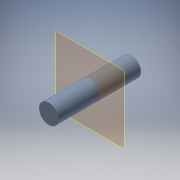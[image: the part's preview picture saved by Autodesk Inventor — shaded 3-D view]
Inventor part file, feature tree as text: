
AUTODESK INVENTOR PART (.ipt)
format: ipt  version: 2019 (Build 230136000, 136)  size: 96,256 bytes
history: native  units: mm
features: other x4, extrude x1, sketch x1, reference x1
ambient origin geometry x8: Origin, YZ Plane, XZ Plane, XY Plane, X Axis, Y Axis, Z Axis, Center Point
bodies: Body1 (feature_tree)
feature tree (7):
  other  "作業平面1"
  extrude  "押し出し2"  Depth=0.3mm
  sketch  "スケッチ2"
  reference  "参照2"
  other  "<userpath>\OneDrive\デスクトップ\mini_robot\mini_robot.iam"
  other  "mini_robot.iam"
  other  "head:1"
